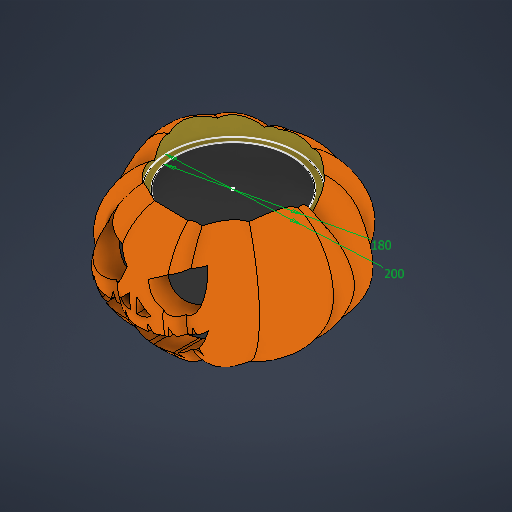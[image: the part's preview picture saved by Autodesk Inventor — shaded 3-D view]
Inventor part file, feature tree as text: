
AUTODESK INVENTOR PART (.ipt)
format: ipt  version: 2025.1 (Build 291241020, 241B)  size: 1,517,568 bytes
history: native  units: in
note: dims shown in document units (in); Inventor stores cm internally (conversion verified against a paired STEP export)
features: other x14, extrude x3, sketch x2
ambient origin geometry x8: Origin, YZ Plane, XZ Plane, XY Plane, X Axis, Y Axis, Z Axis, Center Point
bodies: Solid1 (feature_tree)
feature tree (19):
  other  "Axe1"
  other  "Plan1"
  other  "Plan2"
  other  "Plan3"
  other  "Plan4"
  other  "Plan5"
  other  "Plan6"
  other  "Plan7"
  other  "Plan8"
  other  "Plan9"
  other  "Plan10"
  other  "Plan11"
  other  "Plan12"
  extrude  "Extrusion1"  Depth=3.937in TaperAngle=0.0deg
  sketch  "Sketch3"  dims[d9=0.9781in d10=0.0in d11=7.0866in d12=7.874in d13=3.812in d14=0.0in d15=3.812in d16=0.0in d3=0.0197in d4=0.0344in d5=0.0197in d6=0.0344in d7=0.0197in d8=0.0344in]
  extrude  "Extrusion3"  Depth=7.0866in
  extrude  "Extrusion4"  Depth=7.874in
  sketch  "Sketch1"  dims[d0=7.874in d1=3.937in d2=0.0in]
  other  "Enlèv. mat.-Extru.2"
